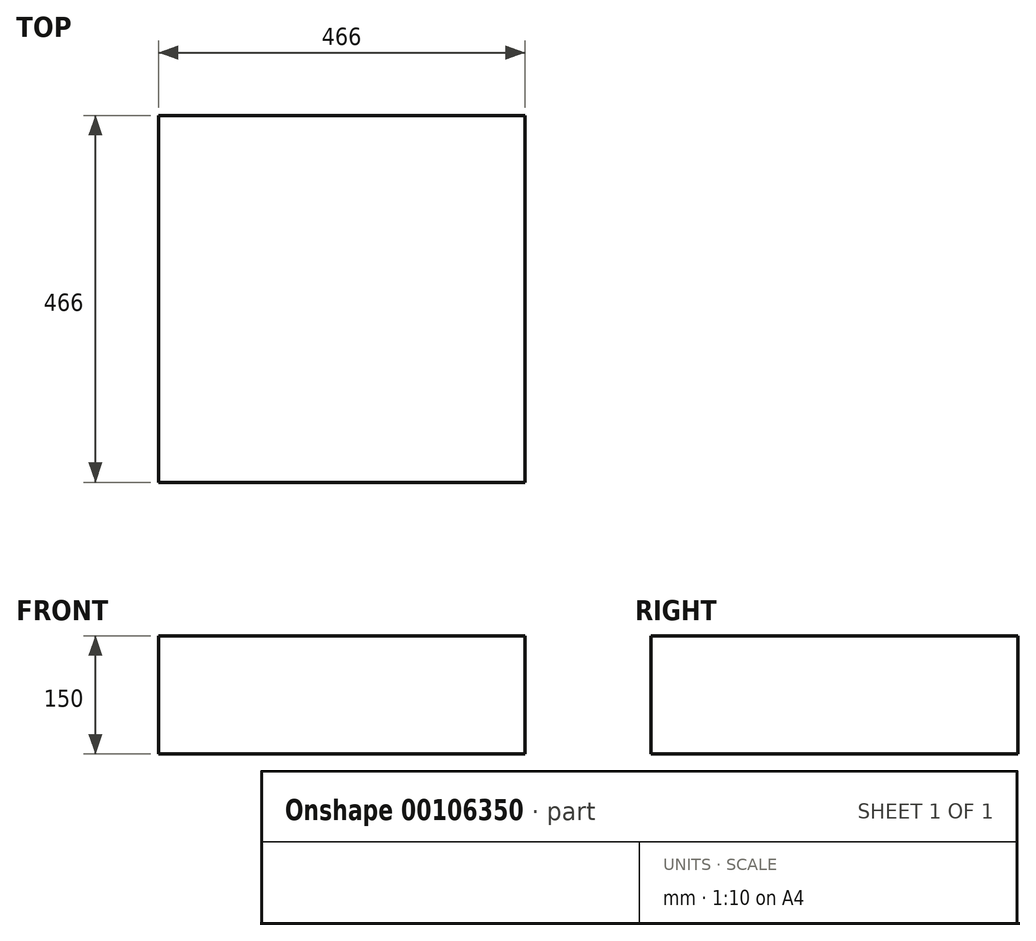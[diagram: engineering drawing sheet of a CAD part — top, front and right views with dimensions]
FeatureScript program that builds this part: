
annotation { "Feature Type Name" : "Feature", "Feature Type Description" : "" }
export const myFeature = defineFeature(function(context is Context, id is Id, definition is map)
    precondition{}
    {
        {
            var Q0;
            Q0=qCreatedBy(makeId("Top.planeOp"),FACE);
            var sketch = newSketch(context, id + "F0", { "sketchPlane" : qUnion([Q0])});
            skLineSegment(sketch, "E0.bottom", {"start": v(-233, 233) * mm, "end": v(233, 233) * mm});
            skLineSegment(sketch, "E0.top", {"start": v(-233, -233) * mm, "end": v(233, -233) * mm});
            skLineSegment(sketch, "E0.left", {"start": v(-233, 233) * mm, "end": v(-233, -233) * mm});
            skLineSegment(sketch, "E0.right", {"start": v(233, 233) * mm, "end": v(233, -233) * mm});
            skSolve(sketch);
        }
        {
            var Q0;
            Q0 = qSketchRegion(id + "F0", true);
            extrude(context, id + "F1", {"entities" : qUnion([Q0]), "endBound" : BoundingType.SYMMETRIC, "depth" : 150 * mm});
        }
        {
            var Q0;
            Q0=makeQuery(id+"F1.opExtrude","CAP_FACE",FACE,{"disambiguationData":[OSD([sQuery(id+"F0.wireOp",EDGE,"E0.bottom"),sQuery(id+"F0.wireOp",EDGE,"E0.top"),sQuery(id+"F0.wireOp",EDGE,"E0.left"),sQuery(id+"F0.wireOp",EDGE,"E0.right")])],"isStart":false});
            var sketch = newSketch(context, id + "F2", { "sketchPlane" : qUnion([Q0])});
            skCircle(sketch, "E1", {"center": v(0, 0) * mm, "radius": 150 * mm});
            skSolve(sketch);
        }
        {
            var Q0;
            Q0 = qSketchRegion(id + "F2", true);
            extrude(context, id + "F3", {"entities" : qUnion([Q0]), "operationType" : NewBodyOperationType.ADD, "oppositeDirection" : true, "depth" : 25 * mm});
        }
    });
